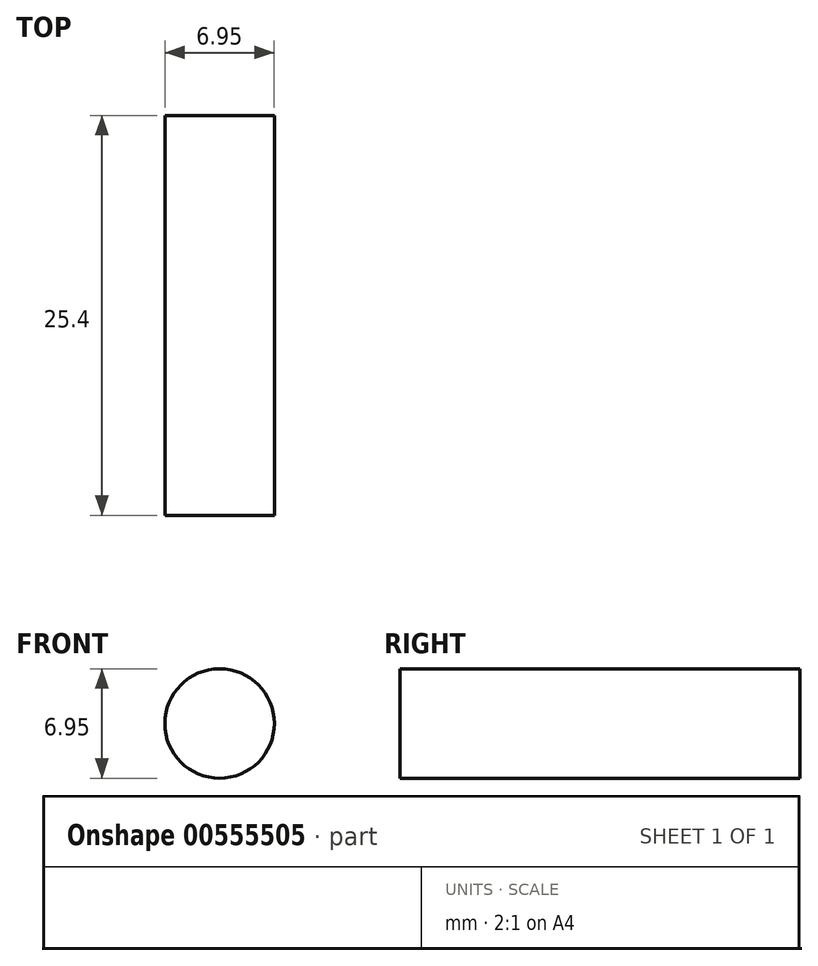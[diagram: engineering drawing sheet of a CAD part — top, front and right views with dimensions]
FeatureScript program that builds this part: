
annotation { "Feature Type Name" : "Feature", "Feature Type Description" : "" }
export const myFeature = defineFeature(function(context is Context, id is Id, definition is map)
    precondition{}
    {
        {
            var Q0;
            Q0=qCreatedBy(makeId("Front.planeOp"),FACE);
            var sketch = newSketch(context, id + "F0", { "sketchPlane" : qUnion([Q0])});
            skLineSegment(sketch, "E0", {"start": v(-30.35, 47.47) * mm, "end": v(-30.35, 31.45) * mm});
            skLineSegment(sketch, "E1", {"start": v(-30.35, 31.45) * mm, "end": v(-34.48, 27.07) * mm});
            skLineSegment(sketch, "E2", {"start": v(-30.35, 31.45) * mm, "end": v(-27.68, 25.86) * mm});
            skLineSegment(sketch, "E3", {"start": v(-30.35, 47.47) * mm, "end": v(-42.25, 39.22) * mm});
            skLineSegment(sketch, "E4", {"start": v(-30.35, 47.47) * mm, "end": v(-18.21, 55.9) * mm});
            skCircle(sketch, "E5", {"center": v(-30.35, 47.47) * mm, "radius": 3.48 * mm});
            skSolve(sketch);
        }
        {
            var Q0;
            {var subQ1=sQuery(id+"F0.wireOp",EDGE,"E0");var subQ3=sQuery(id+"F0.wireOp",EDGE,"E5");var subQ4=makeQuery(id+"F0.imprint","INTERSECT",VERTEX,{"derivedFrom":[subQ1,subQ3]});Q0=makeQuery(id+"F0.imprint","IMPRINT",FACE,{"disambiguationData":[TD([[makeQuery(id+"F0.imprint","IMPRINT",EDGE,{"disambiguationData":[TD([[subQ4,-1.0]])],"derivedFrom":subQ3}),1.0]])]});}
            var Q1;
            {var subQ1=sQuery(id+"F0.wireOp",EDGE,"E3");var subQ3=sQuery(id+"F0.wireOp",EDGE,"E5");var subQ4=makeQuery(id+"F0.imprint","INTERSECT",VERTEX,{"derivedFrom":[subQ1,subQ3]});Q1=makeQuery(id+"F0.imprint","IMPRINT",FACE,{"disambiguationData":[TD([[makeQuery(id+"F0.imprint","IMPRINT",EDGE,{"disambiguationData":[TD([[subQ4,1.0]])],"derivedFrom":subQ3}),1.0]])]});}
            var Q2;
            {var subQ1=sQuery(id+"F0.wireOp",EDGE,"E0");var subQ3=sQuery(id+"F0.wireOp",EDGE,"E5");var subQ4=makeQuery(id+"F0.imprint","INTERSECT",VERTEX,{"derivedFrom":[subQ1,subQ3]});Q2=makeQuery(id+"F0.imprint","IMPRINT",FACE,{"disambiguationData":[TD([[makeQuery(id+"F0.imprint","IMPRINT",EDGE,{"disambiguationData":[TD([[subQ4,1.0]])],"derivedFrom":subQ3}),1.0]])]});}
            extrude(context, id + "F1", {"entities" : qUnion([Q0, Q1, Q2]), "depth" : 25.4 * mm, "offsetDistance" : 25.4 * mm});
        }
    });
